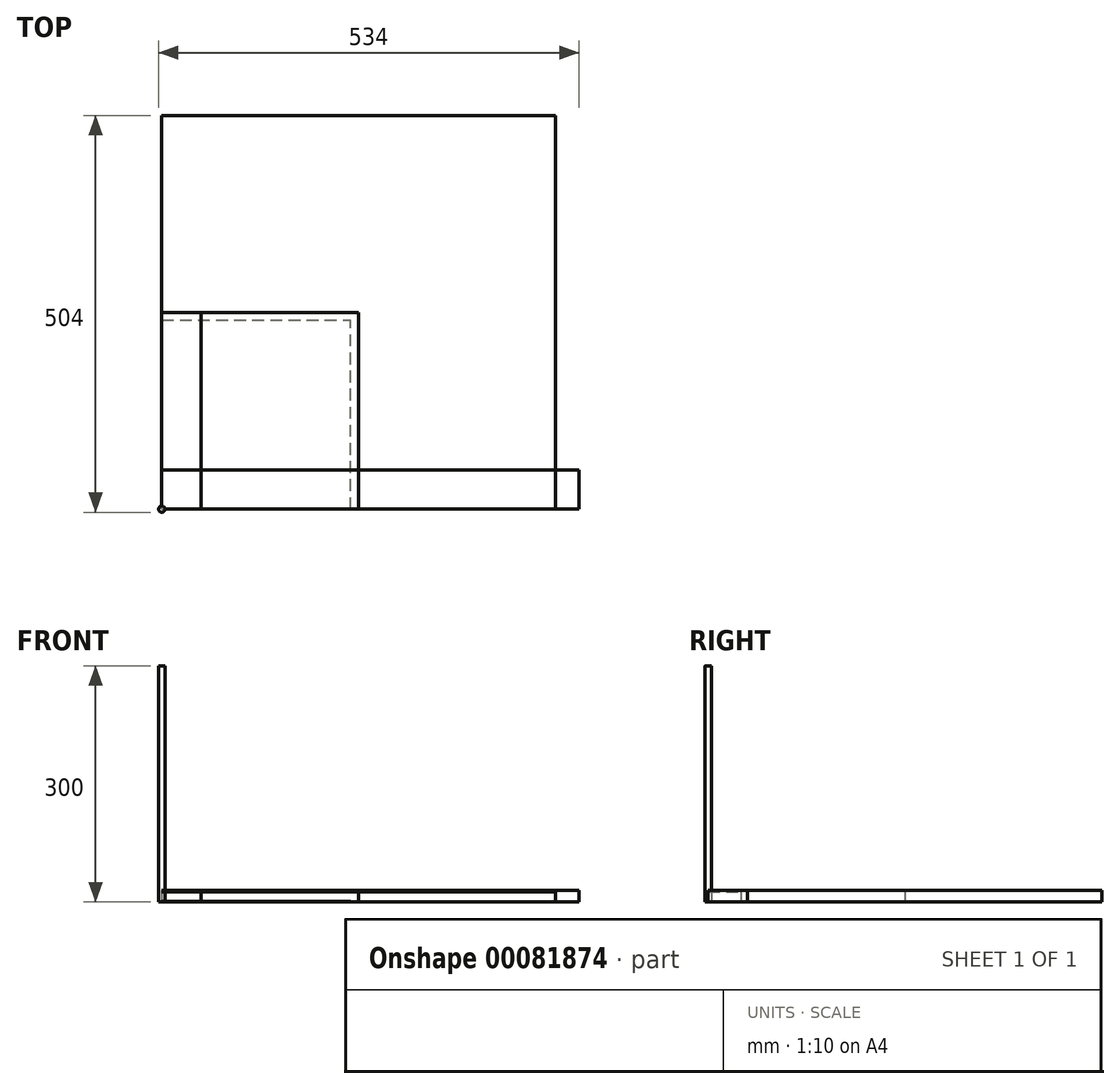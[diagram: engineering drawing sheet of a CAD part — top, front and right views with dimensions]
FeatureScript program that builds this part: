
annotation { "Feature Type Name" : "Feature", "Feature Type Description" : "" }
export const myFeature = defineFeature(function(context is Context, id is Id, definition is map)
    precondition{}
    {
        {
            var Q0;
            Q0=qCreatedBy(makeId("Top.planeOp"),FACE);
            var sketch = newSketch(context, id + "F0", { "sketchPlane" : qUnion([Q0])});
            skCircle(sketch, "E0", {"center": v(0, 0) * mm, "radius": 4 * mm});
            skSolve(sketch);
        }
        {
            var Q0;
            Q0 = qSketchRegion(id + "F0", true);
            extrude(context, id + "F1", {"entities" : qUnion([Q0]), "depth" : 300 * mm});
        }
        {
            var Q0;
            Q0=qCreatedBy(makeId("Top.planeOp"),FACE);
            var sketch = newSketch(context, id + "F2", { "sketchPlane" : qUnion([Q0])});
            skLineSegment(sketch, "E1.bottom", {"start": v(0, 0) * mm, "end": v(500, 0) * mm});
            skLineSegment(sketch, "E1.top", {"start": v(0, 42) * mm, "end": v(500, 42) * mm});
            skLineSegment(sketch, "E1.left", {"start": v(0, 0) * mm, "end": v(0, 42) * mm});
            skLineSegment(sketch, "E1.right", {"start": v(500, 0) * mm, "end": v(500, 42) * mm});
            skSolve(sketch);
        }
        {
            var Q0;
            Q0 = qSketchRegion(id + "F2", true);
            extrude(context, id + "F3", {"entities" : qUnion([Q0]), "depth" : 13 * mm});
        }
        {
            var Q0;
            Q0=qCreatedBy(makeId("Top.planeOp"),FACE);
            var sketch = newSketch(context, id + "F4", { "sketchPlane" : qUnion([Q0])});
            skLineSegment(sketch, "E2.bottom", {"start": v(0, 0) * mm, "end": v(500, 0) * mm});
            skLineSegment(sketch, "E2.top", {"start": v(0, 500) * mm, "end": v(500, 500) * mm});
            skLineSegment(sketch, "E2.left", {"start": v(0, 0) * mm, "end": v(0, 500) * mm});
            skLineSegment(sketch, "E2.right", {"start": v(500, 0) * mm, "end": v(500, 500) * mm});
            skSolve(sketch);
        }
        {
            var Q0;
            Q0 = qSketchRegion(id + "F4", true);
            extrude(context, id + "F5", {"entities" : qUnion([Q0]), "depth" : 15 * mm});
        }
        {
            var Q0;
            Q0=qCreatedBy(makeId("Top.planeOp"),FACE);
            var sketch = newSketch(context, id + "F6", { "sketchPlane" : qUnion([Q0])});
            skLineSegment(sketch, "E3.bottom", {"start": v(0, 0) * mm, "end": v(240, 0) * mm});
            skLineSegment(sketch, "E3.top", {"start": v(0, 240) * mm, "end": v(240, 240) * mm});
            skLineSegment(sketch, "E3.left", {"start": v(0, 0) * mm, "end": v(0, 240) * mm});
            skLineSegment(sketch, "E3.right", {"start": v(240, 0) * mm, "end": v(240, 240) * mm});
            skSolve(sketch);
        }
        {
            var Q0;
            Q0 = qSketchRegion(id + "F6", true);
            extrude(context, id + "F7", {"entities" : qUnion([Q0]), "depth" : 1 * mm});
        }
        {
            var Q0;
            Q0=qCreatedBy(makeId("Top.planeOp"),FACE);
            var sketch = newSketch(context, id + "F8", { "sketchPlane" : qUnion([Q0])});
            skLineSegment(sketch, "E4.bottom", {"start": v(0, 0) * mm, "end": v(50, 0) * mm});
            skLineSegment(sketch, "E4.top", {"start": v(0, 250) * mm, "end": v(50, 250) * mm});
            skLineSegment(sketch, "E4.left", {"start": v(0, 0) * mm, "end": v(0, 250) * mm});
            skLineSegment(sketch, "E4.right", {"start": v(50, 0) * mm, "end": v(50, 250) * mm});
            skSolve(sketch);
        }
        {
            var Q0;
            Q0=makeQuery(id+"F8.imprint","IMPRINT",FACE,{"disambiguationData":[TD([[makeQuery(id+"F8.imprint","IMPRINT",EDGE,{"derivedFrom":sQuery(id+"F8.wireOp",EDGE,"oU4fNsBS-gKnO-oIPi-5JeY-5XoIHaoOnR3z.bottom")}),-1.0]])]});
            var Q1;
            Q1=makeQuery(id+"F8.imprint","IMPRINT",FACE,{"disambiguationData":[TD([[makeQuery(id+"F8.imprint","IMPRINT",EDGE,{"derivedFrom":sQuery(id+"F8.wireOp",EDGE,"E4.bottom")}),1.0]])]});
            extrude(context, id + "F9", {"entities" : qUnion([Q0, Q1]), "depth" : 15 * mm});
        }
        {
            var Q0;
            Q0=qCreatedBy(makeId("Top.planeOp"),FACE);
            var sketch = newSketch(context, id + "F10", { "sketchPlane" : qUnion([Q0])});
            skLineSegment(sketch, "E5.bottom", {"start": v(0, 0) * mm, "end": v(530, 0) * mm});
            skLineSegment(sketch, "E5.top", {"start": v(0, 50) * mm, "end": v(530, 50) * mm});
            skLineSegment(sketch, "E5.left", {"start": v(0, 0) * mm, "end": v(0, 50) * mm});
            skLineSegment(sketch, "E5.right", {"start": v(530, 0) * mm, "end": v(530, 50) * mm});
            skSolve(sketch);
        }
        {
            var Q0;
            Q0=makeQuery(id+"F10.imprint","IMPRINT",FACE,{"disambiguationData":[TD([[makeQuery(id+"F10.imprint","IMPRINT",EDGE,{"derivedFrom":sQuery(id+"F10.wireOp",EDGE,"E5.bottom")}),1.0]])]});
            extrude(context, id + "F11", {"entities" : qUnion([Q0]), "depth" : 15 * mm});
        }
        {
            var Q0;
            Q0=qCreatedBy(makeId("Top.planeOp"),FACE);
            var sketch = newSketch(context, id + "F12", { "sketchPlane" : qUnion([Q0])});
            skLineSegment(sketch, "E6.bottom", {"start": v(0, 0) * mm, "end": v(250, 0) * mm});
            skLineSegment(sketch, "E6.top", {"start": v(0, 250) * mm, "end": v(250, 250) * mm});
            skLineSegment(sketch, "E6.left", {"start": v(0, 0) * mm, "end": v(0, 250) * mm});
            skLineSegment(sketch, "E6.right", {"start": v(250, 0) * mm, "end": v(250, 250) * mm});
            skSolve(sketch);
        }
        {
            var Q0;
            Q0 = qSketchRegion(id + "F12", true);
            extrude(context, id + "F13", {"entities" : qUnion([Q0]), "depth" : 15 * mm});
        }
        {
            var Q0;
            Q0=qCreatedBy(makeId("Top.planeOp"),FACE);
            var sketch = newSketch(context, id + "F14", { "sketchPlane" : qUnion([Q0])});
            skLineSegment(sketch, "E7.bottom", {"start": v(0, 0) * mm, "end": v(500, 0) * mm});
            skLineSegment(sketch, "E7.top", {"start": v(0, 50) * mm, "end": v(500, 50) * mm});
            skLineSegment(sketch, "E7.left", {"start": v(0, 0) * mm, "end": v(0, 50) * mm});
            skLineSegment(sketch, "E7.right", {"start": v(500, 0) * mm, "end": v(500, 50) * mm});
            skSolve(sketch);
        }
        {
            var Q0;
            Q0=makeQuery(id+"F14.imprint","IMPRINT",FACE,{"disambiguationData":[TD([[makeQuery(id+"F14.imprint","IMPRINT",EDGE,{"derivedFrom":sQuery(id+"F14.wireOp",EDGE,"E7.bottom")}),1.0]])]});
            extrude(context, id + "F15", {"entities" : qUnion([Q0]), "depth" : 15 * mm});
        }
    });
